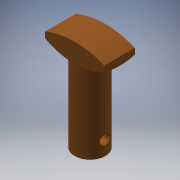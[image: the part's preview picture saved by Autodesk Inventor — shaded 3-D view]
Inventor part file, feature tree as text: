
AUTODESK INVENTOR PART (.ipt)
format: ipt  version: 2018 (Build 220112000, 112)  size: 159,744 bytes
history: native  units: mm (DEFAULTED — no unit token found)
features: sketch x3, extrude x3, plane x2, revolve x1
ambient origin geometry x8: Origin, YZ Plane, XZ Plane, XY Plane, X Axis, Y Axis, Z Axis, Center Point
bodies: Solid1 (feature_tree)
feature tree (9):
  sketch  "Sketch1"  dims[d0=32.0mm d1=8.0mm]
  extrude  "Extrusion1"  Depth=32.0mm
  revolve  "Revolution1"  [1 undecoded]
  plane  "Work Plane1"
  plane  "Work Plane2"
  extrude  "Extrusion2"  Depth=4.0mm
  extrude  "Extrusion3"  TaperAngle=90.0deg  [1 undecoded]
  sketch  "Sketch2"  dims[d2=25.0mm d3=13.0mm d4=0.0mm]
  sketch  "Sketch3"  dims[d5=27.0mm d6=50.0mm d7=90.0deg d8=42.0mm d9=13.0mm d10=0.0mm d11=4.0mm d12=6.0mm d13=13.0mm d14=0.0mm]
note: 2 required parameter values undecoded (feature->parameter linkage not recoverable at this tier; creation-order binding heuristic only, values carry confidence <= 0.55)